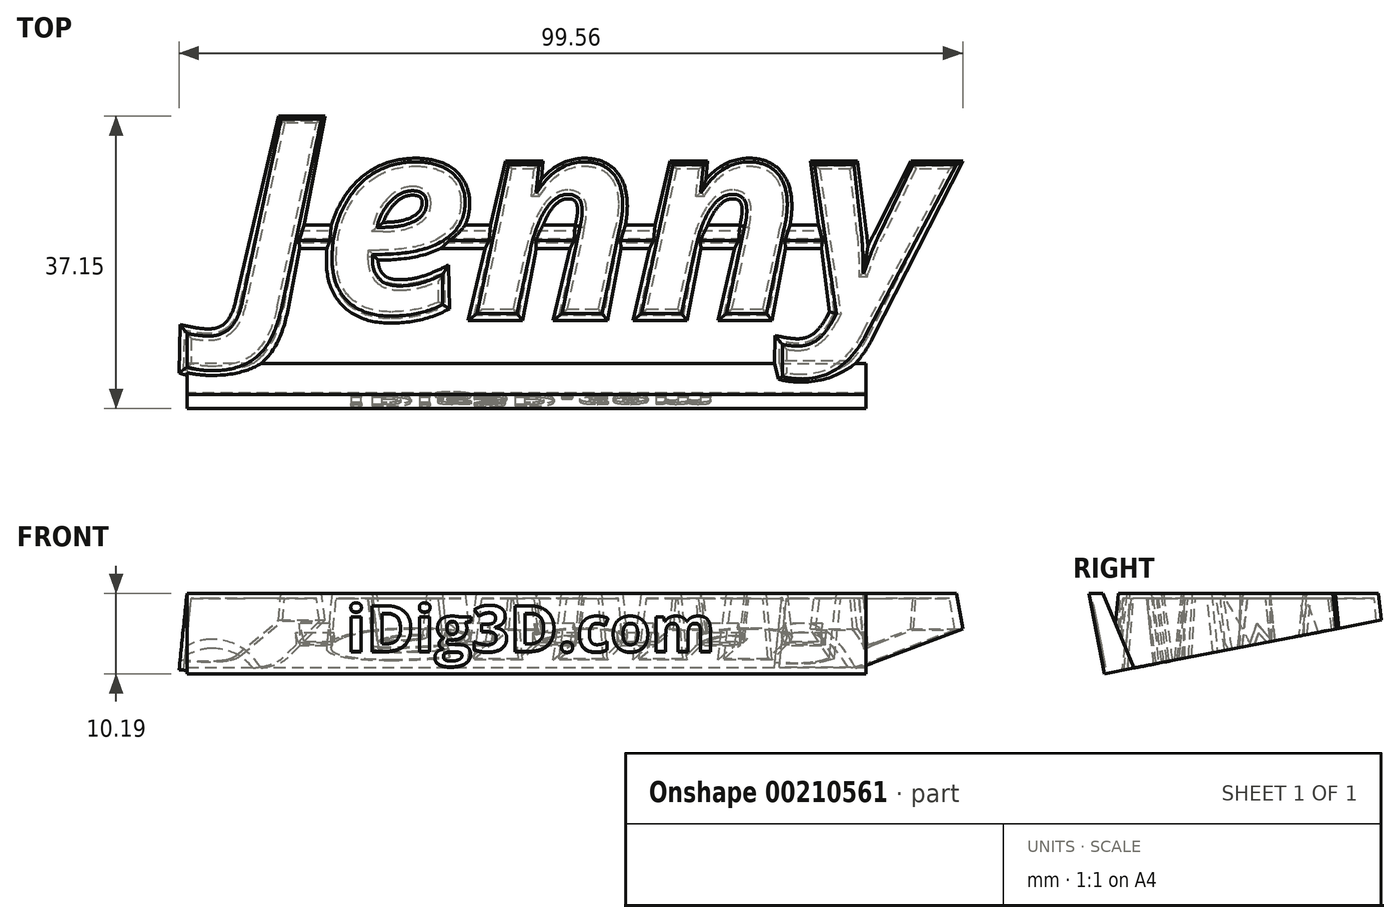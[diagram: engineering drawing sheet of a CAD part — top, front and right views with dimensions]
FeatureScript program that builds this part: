
annotation { "Feature Type Name" : "Feature", "Feature Type Description" : "" }
export const myFeature = defineFeature(function(context is Context, id is Id, definition is map)
    precondition{}
    {
        {
            var Q0;
            Q0=qCreatedBy(makeId("Top.planeOp"),FACE);
            var sketch = newSketch(context, id + "F0", { "sketchPlane" : qUnion([Q0])});
            skText(sketch, "E0", { "text": "Jenny", "fontName": "OpenSans-BoldItalic.ttf"});
            const initialGuessF0  = {"E0": [-0.05047, -0.00023, 1, 0, 0.02492]};
            skSetInitialGuess(sketch, initialGuessF0);
            skSolve(sketch);
        }
        {
            var Q0;
            Q0=qSketchRegion(id+"F0",true);
            extrude(context, id + "F1", {"entities" : qUnion([Q0]), "oppositeDirection" : true, "depth" : 10 * mm, "hasDraft" : true, "draftAngle" : 6 * degree});
        }
        {
            var Q0;
            Q0=qCreatedBy(makeId("Right.planeOp"),FACE);
            var sketch = newSketch(context, id + "F2", { "sketchPlane" : qUnion([Q0])});
            skLineSegment(sketch, "E1.1", {"start": v(-9.37, -10) * mm, "end": v(-8.32, 0) * mm});
            skLineSegment(sketch, "E2", {"start": v(-12.32, 0) * mm, "end": v(-10.35, -10.2) * mm});
            skLineSegment(sketch, "E3", {"start": v(-10.35, -10.2) * mm, "end": v(25.06, -3.33) * mm});
            skLineSegment(sketch, "E4.0", {"start": v(25.76, -10) * mm, "end": v(25.41, -6.67) * mm});
            skLineSegment(sketch, "E5", {"start": v(-8.84, -5) * mm, "end": v(-9.37, -10) * mm});
            skLineSegment(sketch, "E6", {"start": v(-10.35, -10) * mm, "end": v(-10.35, -10.2) * mm});
            skLineSegment(sketch, "E7", {"start": v(-10.35, -10) * mm, "end": v(25.76, -10) * mm});
            skLineSegment(sketch, "E8", {"start": v(25.06, -3.33) * mm, "end": v(24.7, 0) * mm});
            skLineSegment(sketch, "E9", {"start": v(25.41, -6.67) * mm, "end": v(25.06, -3.33) * mm});
            skLineSegment(sketch, "E10", {"start": v(-12.32, 0) * mm, "end": v(-10.92, 0) * mm});
            skLineSegment(sketch, "E11", {"start": v(-10.92, 0) * mm, "end": v(-6.96, -9.53) * mm, "construction": true});
            skLineSegment(sketch, "E12", {"start": v(-6.59, -9.46) * mm, "end": v(-10.52, 0) * mm});
            skLineSegment(sketch, "E13", {"start": v(-10.52, 0) * mm, "end": v(-10.92, 0) * mm});
            skSolve(sketch);
        }
        {
            var Q0;
            {var subQ4=sQuery(id+"F2.wireOp",EDGE,"E4.0");Q0=makeQuery(id+"F2.imprint","IMPRINT",FACE,{"disambiguationData":[TD([[makeQuery(id+"F2.imprint","IMPRINT",EDGE,{"derivedFrom":subQ4}),1.0]])]});}
            var Q1;
            Q1=makeQuery(id+"F1.opExtrude","SWEPT_FACE",FACE,{"disambiguationData":[OSD([sQuery(id+"F0.wireOp",EDGE,"d4536f9c-434f-49d7-b92b-0fbf4eb391be.sketch_text.stroke-78")])]});
            var Q2;
            Q2=makeQuery(id+"F1.opExtrude","CAP_VERTEX",VERTEX,{"disambiguationData":[OSD([sQuery(id+"F0.wireOp",EDGE,"E0.sketch_text.stroke-75"),sQuery(id+"F0.wireOp",EDGE,"E0.sketch_text.stroke-76")])],"isStart":false});
            var Q3;
            Q3=makeQuery(id+"F1.opExtrude","CAP_VERTEX",VERTEX,{"disambiguationData":[OSD([sQuery(id+"F0.wireOp",EDGE,"E0.sketch_text.stroke-1"),sQuery(id+"F0.wireOp",EDGE,"E0.sketch_text.stroke-2")])],"isStart":false});
            extrude(context, id + "F3", {"entities" : qUnion([Q0]), "operationType" : NewBodyOperationType.REMOVE, "endBound" : BoundingType.UP_TO_VERTEX, "endBoundEntityFace" : qUnion([Q1]), "endBoundEntityVertex" : qUnion([Q2]), "depth" : 25 * mm, "hasSecondDirection" : true, "secondDirectionBound" : SecondDirectionBoundingType.UP_TO_VERTEX, "secondDirectionOppositeDirection" : true, "secondDirectionBoundEntityVertex" : qUnion([Q3]), "secondDirectionDepth" : 25 * mm});
        }
        {
            var Q0;
            Q0=makeQuery(id+"F3.boolean.opBoolean","COPY",FACE,{"disambiguationData":[TD([makeQuery(id+"F1.opExtrude","SWEPT_FACE",FACE,{"disambiguationData":[OSD([sQuery(id+"F0.wireOp",EDGE,"E0.sketch_text.stroke-51")])]})])],"derivedFrom":makeQuery(id+"F3.opExtrude","SWEPT_FACE",FACE,{"disambiguationData":[OSD([sQuery(id+"F2.wireOp",EDGE,"E3")])]})});
            var sketch = newSketch(context, id + "F4", { "sketchPlane" : qUnion([Q0])});
            skLineSegment(sketch, "E14.bottom", {"start": v(-45.45, -6.63) * mm, "end": v(29.06, -6.63) * mm});
            skLineSegment(sketch, "E14.top", {"start": v(-45.45, -9.63) * mm, "end": v(29.06, -9.63) * mm});
            skLineSegment(sketch, "E14.left", {"start": v(-45.45, -6.63) * mm, "end": v(-45.45, -9.63) * mm});
            skLineSegment(sketch, "E14.right", {"start": v(29.06, -6.63) * mm, "end": v(29.06, -9.63) * mm});
            skPoint(sketch, "E14.middle", {"position": v(-8.2, -8.13) * mm});
            skSolve(sketch);
        }
        {
            var Q0;
            Q0 = qSketchRegion(id + "F4", true);
            extrude(context, id + "F5", {"entities" : qUnion([Q0]), "operationType" : NewBodyOperationType.ADD, "oppositeDirection" : true, "depth" : 4 * mm, "hasDraft" : true, "draftAngle" : 30 * degree, "draftPullDirection" : true});
        }
        {
            var Q0;
            {var subQ0=makeQuery(id+"F3.opExtrude","SWEPT_FACE",FACE,{"disambiguationData":[OSD([sQuery(id+"F2.wireOp",EDGE,"E3")])]});Q0=makeQuery(id+"F5.boolean.opBoolean","MERGE",FACE,{"derivedFrom":[makeQuery(id+"F3.boolean.opBoolean","COPY",FACE,{"disambiguationData":[TD([makeQuery(id+"F1.opExtrude","SWEPT_FACE",FACE,{"disambiguationData":[OSD([sQuery(id+"F0.wireOp",EDGE,"E0.sketch_text.stroke-0")])]})])],"derivedFrom":subQ0}),makeQuery(id+"F3.boolean.opBoolean","COPY",FACE,{"disambiguationData":[TD([makeQuery(id+"F1.opExtrude","SWEPT_FACE",FACE,{"disambiguationData":[OSD([sQuery(id+"F0.wireOp",EDGE,"E0.sketch_text.stroke-68")])]})])],"derivedFrom":subQ0}),makeQuery(id+"F3.boolean.opBoolean","COPY",FACE,{"disambiguationData":[TD([makeQuery(id+"F1.opExtrude","SWEPT_FACE",FACE,{"disambiguationData":[OSD([sQuery(id+"F0.wireOp",EDGE,"E0.sketch_text.stroke-34")])]})])],"derivedFrom":subQ0}),makeQuery(id+"F3.boolean.opBoolean","COPY",FACE,{"disambiguationData":[TD([makeQuery(id+"F1.opExtrude","SWEPT_FACE",FACE,{"disambiguationData":[OSD([sQuery(id+"F0.wireOp",EDGE,"E0.sketch_text.stroke-51")])]})])],"derivedFrom":subQ0}),makeQuery(id+"F3.boolean.opBoolean","COPY",FACE,{"disambiguationData":[TD([makeQuery(id+"F1.opExtrude","SWEPT_FACE",FACE,{"disambiguationData":[OSD([sQuery(id+"F0.wireOp",EDGE,"E0.sketch_text.stroke-10")])]})])],"derivedFrom":subQ0}),makeQuery(id+"F5.opExtrude","CAP_FACE",FACE,{"disambiguationData":[OSD([sQuery(id+"F4.wireOp",EDGE,"E14.bottom"),sQuery(id+"F4.wireOp",EDGE,"E14.top"),sQuery(id+"F4.wireOp",EDGE,"E14.left"),sQuery(id+"F4.wireOp",EDGE,"E14.right")])],"isStart":true})]});}
            shell(context, id + "F6", {"entities" : qUnion([Q0]), "thickness" : 0.6 * mm});
        }
        {
            var Q0;
            Q0=makeQuery(id+"F2.imprint","IMPRINT",FACE,{"disambiguationData":[TD([[makeQuery(id+"F2.imprint","IMPRINT",EDGE,{"derivedFrom":sQuery(id+"F2.wireOp",EDGE,"E2")}),1.0]])]});
            var Q1;
            {var subQ0=sQuery(id+"F2.wireOp",EDGE,"E11");var subQ1=sQuery(id+"F2.wireOp",EDGE,"E3");var subQ2=makeQuery(id+"F2.imprint","INTERSECT",VERTEX,{"derivedFrom":[subQ1,subQ0]});Q1=makeQuery(id+"F2.imprint","IMPRINT",FACE,{"disambiguationData":[TD([[makeQuery(id+"F2.imprint","IMPRINT",EDGE,{"disambiguationData":[TD([[subQ2,1.0]])],"derivedFrom":subQ0}),-1.0]])]});}
            var Q2;
            {var subQ0=sQuery(id+"F2.wireOp",EDGE,"E6");Q2=makeQuery(id+"F2.imprint","IMPRINT",FACE,{"disambiguationData":[TD([[makeQuery(id+"F2.imprint","IMPRINT",EDGE,{"derivedFrom":subQ0}),1.0]])]});}
            var Q3;
            {var subQ0=sQuery(id+"F2.wireOp",EDGE,"E1.1");var subQ5=makeQuery(id+"F2.imprint","IMPRINT",VERTEX,{"derivedFrom":subQ0});Q3=makeQuery(id+"F2.imprint","IMPRINT",FACE,{"disambiguationData":[TD([[makeQuery(id+"F2.imprint","IMPRINT",EDGE,{"disambiguationData":[TD([[subQ5,-1.0]])],"derivedFrom":subQ0}),-1.0]])]});}
            var Q4;
            Q4=makeQuery(id+"F1.opExtrude","CAP_VERTEX",VERTEX,{"disambiguationData":[OSD([sQuery(id+"F0.wireOp",EDGE,"E0.sketch_text.stroke-76"),sQuery(id+"F0.wireOp",EDGE,"E0.sketch_text.stroke-77")])],"isStart":true});
            var Q5;
            Q5=makeQuery(id+"F1.opExtrude","CAP_VERTEX",VERTEX,{"disambiguationData":[OSD([sQuery(id+"F0.wireOp",EDGE,"E0.sketch_text.stroke-0"),sQuery(id+"F0.wireOp",EDGE,"E0.sketch_text.stroke-1")])],"isStart":true});
            extrude(context, id + "F7", {"entities" : qUnion([Q0, Q1, Q2, Q3]), "operationType" : NewBodyOperationType.ADD, "endBound" : BoundingType.UP_TO_VERTEX, "endBoundEntityVertex" : qUnion([Q4]), "depth" : 25 * mm, "hasSecondDirection" : true, "secondDirectionBound" : SecondDirectionBoundingType.UP_TO_VERTEX, "secondDirectionOppositeDirection" : true, "secondDirectionBoundEntityVertex" : qUnion([Q5]), "secondDirectionDepth" : 25 * mm});
        }
        {
            var Q0;
            Q0=makeQuery(id+"F7.opExtrude","SWEPT_FACE",FACE,{"disambiguationData":[OSD([sQuery(id+"F2.wireOp",EDGE,"E2")])]});
            var sketch = newSketch(context, id + "F8", { "sketchPlane" : qUnion([Q0])});
            skText(sketch, "E15", { "text": "iDig3D.com", "fontName": "OpenSans-Bold.ttf"});
            skPoint(sketch, "E16", {"position": v(-12.3, 2.34) * mm});
            const initialGuessF8  = {"E15": [-0.03571, -0.0052, 1, 0, 0.006]};
            skSetInitialGuess(sketch, initialGuessF8);
            skSolve(sketch);
        }
        {
            var Q0;
            Q0 = qSketchRegion(id + "F8", true);
            extrude(context, id + "F9", {"entities" : qUnion([Q0]), "operationType" : NewBodyOperationType.REMOVE, "oppositeDirection" : true, "depth" : 0.3 * mm});
        }
    });
